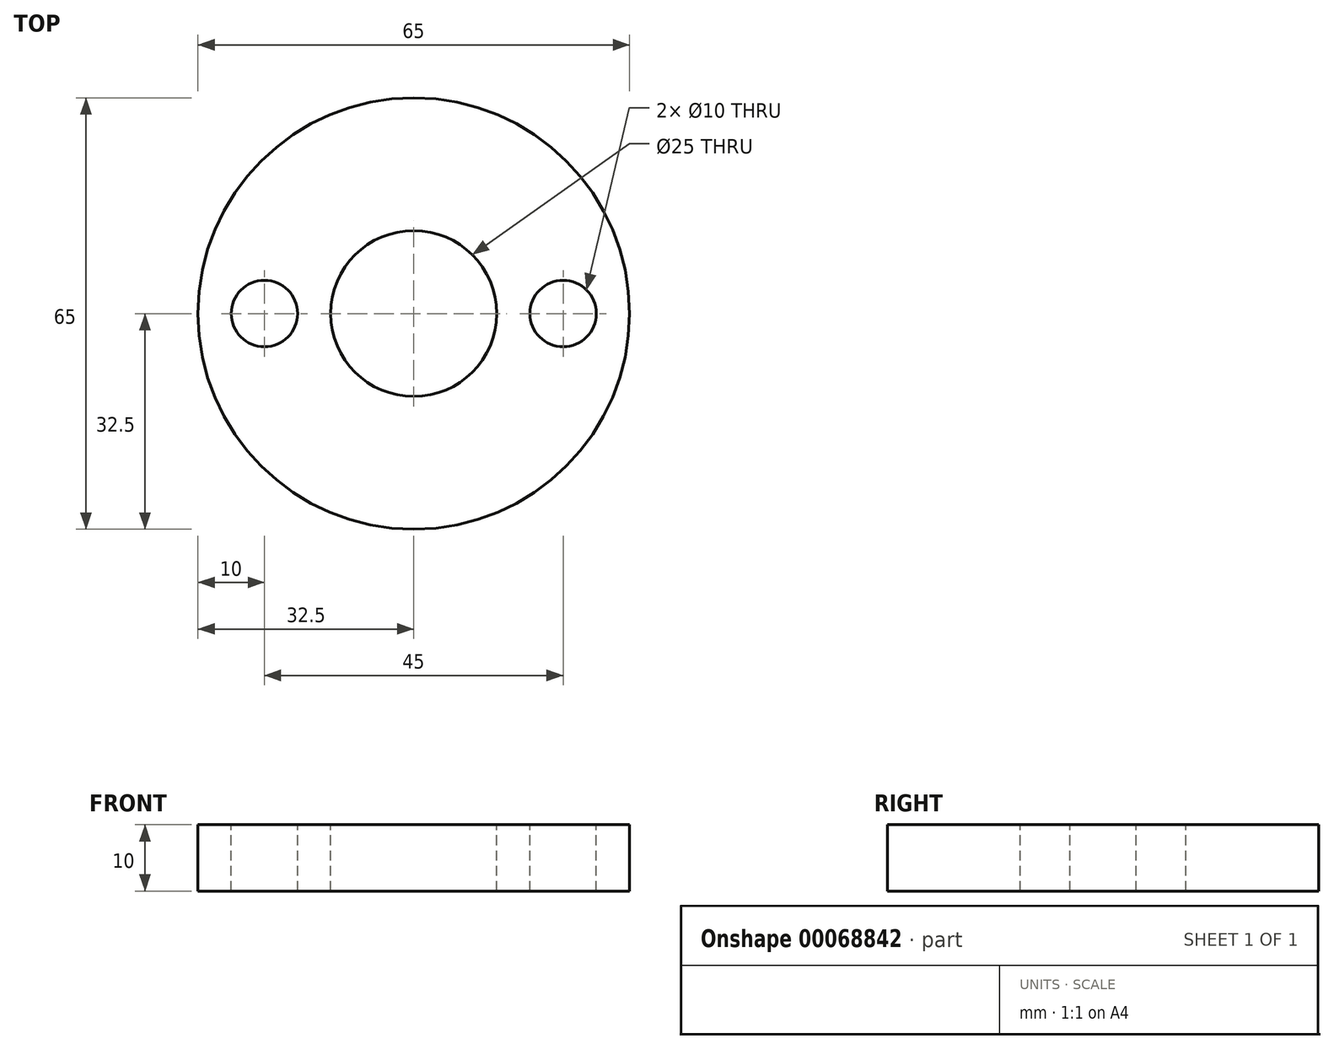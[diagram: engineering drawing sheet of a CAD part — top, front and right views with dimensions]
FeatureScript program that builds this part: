
annotation { "Feature Type Name" : "Feature", "Feature Type Description" : "" }
export const myFeature = defineFeature(function(context is Context, id is Id, definition is map)
    precondition{}
    {
        {
            var Q0;
            Q0=qCreatedBy(makeId("Front.planeOp"),FACE);
            var sketch = newSketch(context, id + "F0", { "sketchPlane" : qUnion([Q0])});
            skLineSegment(sketch, "E0", {"start": v(0, 43.37) * mm, "end": v(0, -43.88) * mm, "construction": true});
            skLineSegment(sketch, "E1.bottom", {"start": v(12.5, 0) * mm, "end": v(32.5, 0) * mm});
            skLineSegment(sketch, "E1.top", {"start": v(12.5, 10) * mm, "end": v(32.5, 10) * mm});
            skLineSegment(sketch, "E1.left", {"start": v(12.5, 0) * mm, "end": v(12.5, 10) * mm});
            skLineSegment(sketch, "E1.right", {"start": v(32.5, 0) * mm, "end": v(32.5, 10) * mm});
            skSolve(sketch);
        }
        {
            var Q0;
            Q0 = qSketchRegion(id + "F0", true);
            var Q1;
            Q1=sQuery(id+"F0.wireOp",EDGE,"E0");
            revolve(context, id + "F1", {"entities" : qUnion([Q0]), "axis" : qUnion([Q1]), "revolveType" : RevolveType.FULL});
        }
        {
            var Q0;
            Q0=makeQuery(id+"F1.opRevolve","SWEPT_FACE",FACE,{"disambiguationData":[OSD([sQuery(id+"F0.wireOp",EDGE,"E1.top")])]});
            var sketch = newSketch(context, id + "F2", { "sketchPlane" : qUnion([Q0])});
            skLineSegment(sketch, "E2", {"start": v(-32.5, 0) * mm, "end": v(-12.5, 0) * mm, "construction": true});
            skLineSegment(sketch, "E3", {"start": v(12.5, 0) * mm, "end": v(32.5, 0) * mm, "construction": true});
            skCircle(sketch, "E4", {"center": v(-22.5, 0) * mm, "radius": 5 * mm});
            skCircle(sketch, "E5", {"center": v(22.5, 0) * mm, "radius": 5 * mm});
            skSolve(sketch);
        }
        {
            var Q0;
            Q0=makeQuery(id+"F2.imprint","IMPRINT",FACE,{"disambiguationData":[TD([[makeQuery(id+"F2.imprint","IMPRINT",EDGE,{"derivedFrom":sQuery(id+"F2.wireOp",EDGE,"E4")}),1.0]])]});
            var Q1;
            Q1=makeQuery(id+"F2.imprint","IMPRINT",FACE,{"disambiguationData":[TD([[makeQuery(id+"F2.imprint","IMPRINT",EDGE,{"derivedFrom":sQuery(id+"F2.wireOp",EDGE,"E5")}),1.0]])]});
            extrude(context, id + "F3", {"entities" : qUnion([Q0, Q1]), "operationType" : NewBodyOperationType.REMOVE, "oppositeDirection" : true, "depth" : 25 * mm});
        }
    });
